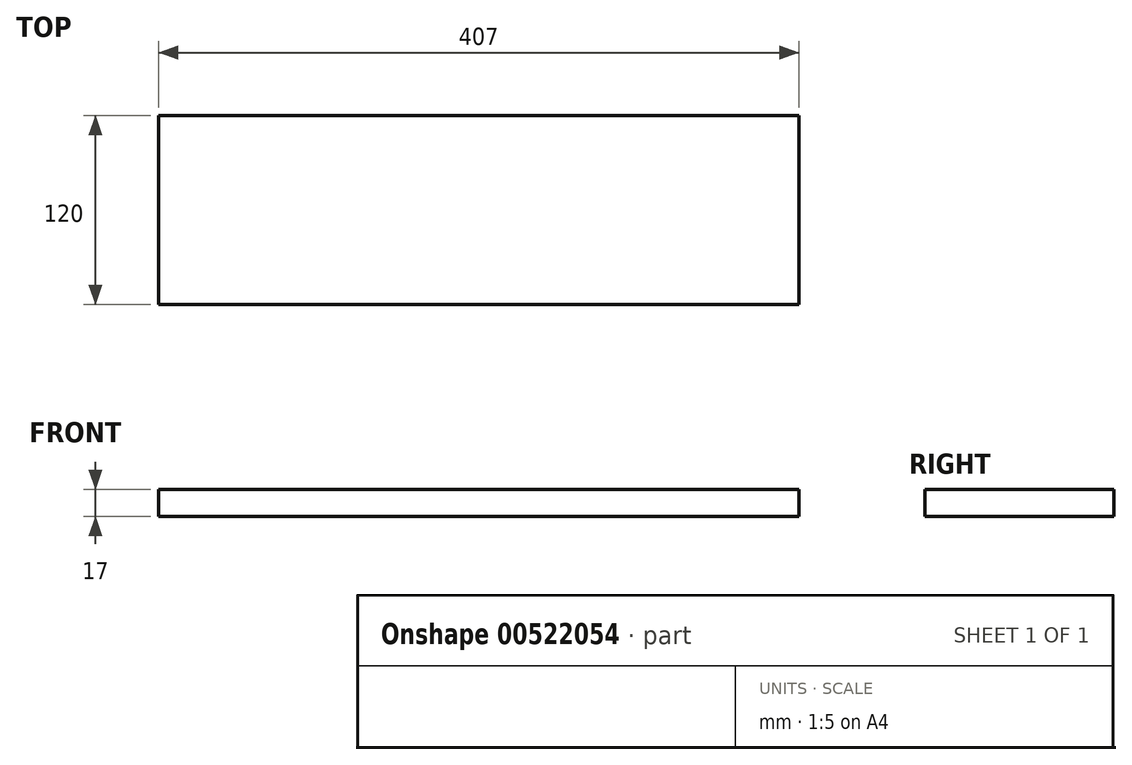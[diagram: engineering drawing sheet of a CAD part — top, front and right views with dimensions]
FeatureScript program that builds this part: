
annotation { "Feature Type Name" : "Feature", "Feature Type Description" : "" }
export const myFeature = defineFeature(function(context is Context, id is Id, definition is map)
    precondition{}
    {
        {
            var Q0;
            Q0=qCreatedBy(makeId("Top.planeOp"),FACE);
            var sketch = newSketch(context, id + "F0", { "sketchPlane" : qUnion([Q0])});
            skLineSegment(sketch, "E0.bottom", {"start": v(0, 0) * mm, "end": v(-407, 0) * mm});
            skLineSegment(sketch, "E0.top", {"start": v(0, 120) * mm, "end": v(-407, 120) * mm});
            skLineSegment(sketch, "E0.left", {"start": v(0, 0) * mm, "end": v(0, 120) * mm});
            skLineSegment(sketch, "E0.right", {"start": v(-407, 0) * mm, "end": v(-407, 120) * mm});
            skSolve(sketch);
        }
        {
            var Q0;
            Q0=makeQuery(id+"F0.imprint","IMPRINT",FACE,{"disambiguationData":[TD([[makeQuery(id+"F0.imprint","IMPRINT",EDGE,{"derivedFrom":sQuery(id+"F0.wireOp",EDGE,"E0.bottom")}),-1.0]])]});
            extrude(context, id + "F1", {"entities" : qUnion([Q0]), "depth" : 17 * mm, "offsetDistance" : 25 * mm});
        }
    });
